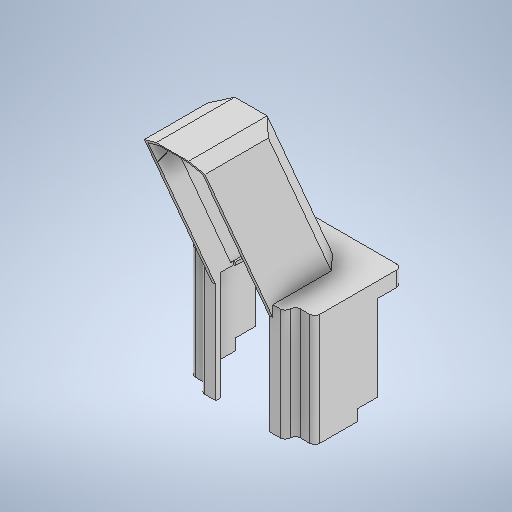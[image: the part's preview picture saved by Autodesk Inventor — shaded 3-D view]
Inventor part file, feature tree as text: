
AUTODESK INVENTOR PART (.ipt)
format: ipt  version: 2025.2 (Build 292293000, 293)  size: 499,200 bytes
history: native  units: in
note: dims shown in document units (in); Inventor stores cm internally (conversion verified against a paired STEP export)
features: extrude x9, sketch x8, chamfer x2, plane x2, fillet x1
ambient origin geometry x8: Origin, YZ Plane, XZ Plane, XY Plane, X Axis, Y Axis, Z Axis, Center Point
bodies: Solid1 (feature_tree)
feature tree (22):
  extrude  "Extrusion1"  Depth=0.1181in
  extrude  "Extrusion2"  Depth=0.0787in
  extrude  "Extrusion3"  Depth=1.9685in
  fillet  "Fillet1"  Radius=0.9843in
  chamfer  "Chamfer1"  Distance=0.4724in
  plane  "Work Plane1"
  extrude  "Extrusion4"  Depth=0.2165in
  chamfer  "Chamfer3"  Distance=0.1181in
  extrude  "Extrusion8"  Depth=0.1969in
  extrude  "Extrusion9"  Depth=0.1378in TaperAngle=45.0deg
  plane  "Work Plane5"
  sketch  "Sketch13"  dims[d19=0.1969in d20=0.2165in]
  extrude  "Extrusion13"  Depth=0.0787in
  extrude  "Extrusion14"  Depth=0.0787in
  extrude  "Extrusion15"  Depth=1.9685in
  sketch  "Sketch1"  dims[d1=2.9577in d2=0.1181in]
  sketch  "Sketch2"  dims[d4=0.1181in d5=0.0in d6=0.0787in]
  sketch  "Sketch3"  dims[d8=4.2323in d9=0.0in d10=1.9685in d11=0.9843in]
  sketch  "Sketch4"  dims[d12=0.9449in]
  sketch  "Sketch9"  dims[d13=0.2165in]
  sketch  "Sketch10"  dims[d15=90.0deg d17=0.4724in d18=0.0in]
  sketch  "Sketch14"  dims[d22=0.1181in d23=0.1181in d27=0.1969in d28=0.1378in d29=0.0787in d30=45.0deg d31=0.0787in d32=0.0787in d33=1.9685in d34=0.5906in d36=2.126in d38=0.1575in d39=2.2835in d40=0.1378in d41=2.3622in d42=5.315in d43=2.1969in d44=0.0in d45=0.0in d47=0.1575in d53=0.5512in d54=0.0787in d55=45.0deg d57=0.1181in d65=0.315in d67=0.3937in d69=0.6201in d70=0.3937in d71=0.7579in d72=0.315in d73=0.1598in d76=0.0787in d77=0.0787in d78=0.7579in d79=0.7579in d80=0.9843in d85=0.6201in d86=0.7579in d90=3.7598in d91=0.0in d92=1.9685in d93=0.7874in d94=0.4331in d95=0.0in d117=1.378in d118=0.3937in d119=0.0in d120=0.3937in d121=0.0in d122=0.3937in d123=0.0in]
